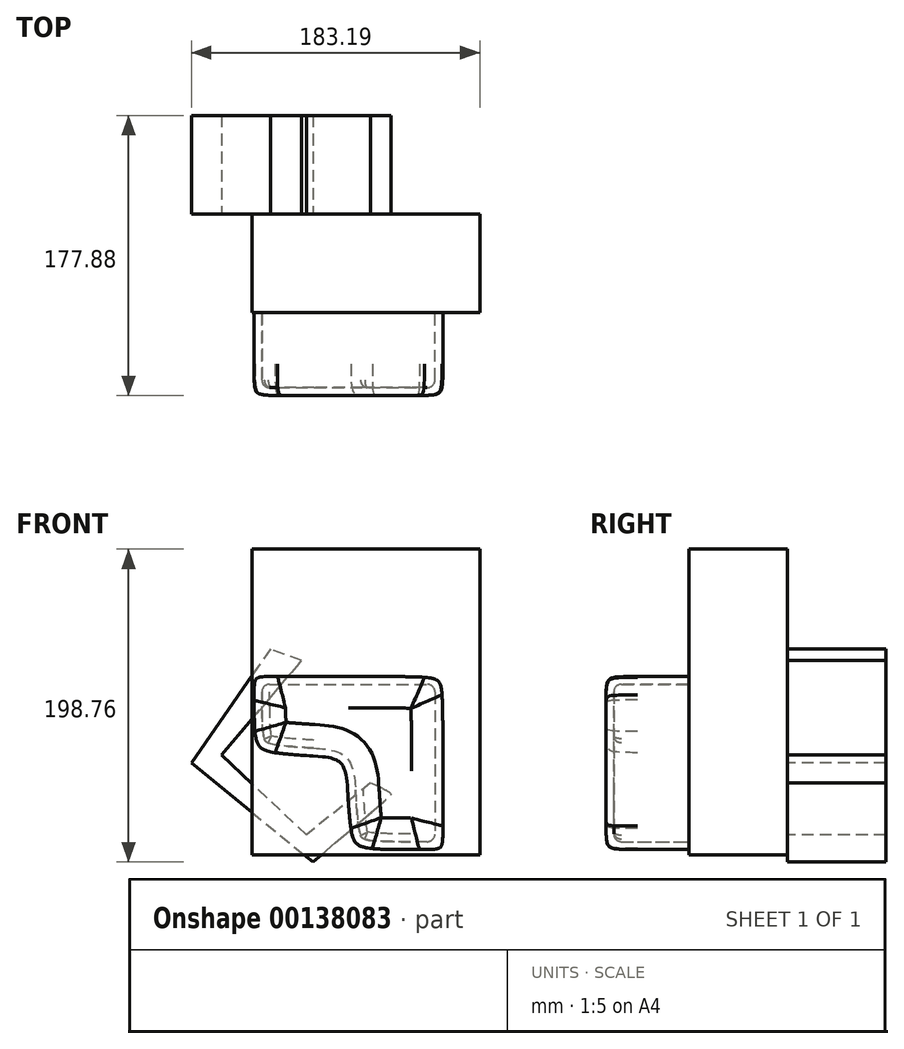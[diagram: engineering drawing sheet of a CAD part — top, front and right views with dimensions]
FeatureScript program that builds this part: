
annotation { "Feature Type Name" : "Feature", "Feature Type Description" : "" }
export const myFeature = defineFeature(function(context is Context, id is Id, definition is map)
    precondition{}
    {
        {
            var Q0;
            Q0=qCreatedBy(makeId("Front.planeOp"),FACE);
            var sketch = newSketch(context, id + "F0", { "sketchPlane" : qUnion([Q0])});
            skLineSegment(sketch, "E0", {"start": v(-60.72, 50) * mm, "end": v(59.28, 50) * mm});
            skLineSegment(sketch, "E1", {"start": v(59.28, 50) * mm, "end": v(59.28, -60) * mm});
            skLineSegment(sketch, "E2", {"start": v(59.28, -60) * mm, "end": v(-0.72, -60) * mm});
            skLineSegment(sketch, "E3", {"start": v(-0.72, -60) * mm, "end": v(-0.72, 0) * mm});
            skLineSegment(sketch, "E4", {"start": v(-0.72, 0) * mm, "end": v(-60.72, 0) * mm});
            skLineSegment(sketch, "E5", {"start": v(-60.72, 0) * mm, "end": v(-60.72, 50) * mm});
            skSolve(sketch);
        }
        {
            var Q0;
            Q0=makeQuery(id+"F0.imprint","IMPRINT",FACE,{"disambiguationData":[TD([[makeQuery(id+"F0.imprint","IMPRINT",EDGE,{"derivedFrom":sQuery(id+"F0.wireOp",EDGE,"E0")}),-1.0]])]});
            extrude(context, id + "F1", {"entities" : qUnion([Q0]), "depth" : 115.18 * mm});
        }
        {
            var Q0;
            Q0=makeQuery(id+"F1.opExtrude","SWEPT_EDGE",EDGE,{"disambiguationData":[OSD([sQuery(id+"F0.wireOp",EDGE,"E3"),sQuery(id+"F0.wireOp",EDGE,"E4")])]});
            fillet(context, id + "F2", {"entities" : qUnion([Q0]), "radius" : 50 * mm, "tangentPropagation" : true, "rho" : .8, "crossSection" : FilletCrossSection.CONIC, "allowEdgeOverflow" : false});
        }
        {
            var Q0;
            Q0=makeQuery(id+"F1.opExtrude","SWEPT_EDGE",EDGE,{"disambiguationData":[OSD([sQuery(id+"F0.wireOp",EDGE,"E2"),sQuery(id+"F0.wireOp",EDGE,"E3")])]});
            fillet(context, id + "F3", {"entities" : qUnion([Q0]), "radius" : 40 * mm, "tangentPropagation" : true, "rho" : .8, "crossSection" : FilletCrossSection.CONIC, "allowEdgeOverflow" : false});
        }
        {
            var Q0;
            Q0=makeQuery(id+"F1.opExtrude","SWEPT_EDGE",EDGE,{"disambiguationData":[OSD([sQuery(id+"F0.wireOp",EDGE,"E4"),sQuery(id+"F0.wireOp",EDGE,"E5")])]});
            fillet(context, id + "F4", {"entities" : qUnion([Q0]), "radius" : 40 * mm, "tangentPropagation" : true, "rho" : .8, "crossSection" : FilletCrossSection.CONIC, "allowEdgeOverflow" : false});
        }
        {
            var Q0;
            Q0=makeQuery(id+"F1.opExtrude","SWEPT_EDGE",EDGE,{"disambiguationData":[OSD([sQuery(id+"F0.wireOp",EDGE,"E0"),sQuery(id+"F0.wireOp",EDGE,"E5")])]});
            fillet(context, id + "F5", {"entities" : qUnion([Q0]), "radius" : 15 * mm, "tangentPropagation" : true, "rho" : .8, "crossSection" : FilletCrossSection.CONIC, "allowEdgeOverflow" : false});
        }
        {
            var Q0;
            Q0=makeQuery(id+"F1.opExtrude","SWEPT_EDGE",EDGE,{"disambiguationData":[OSD([sQuery(id+"F0.wireOp",EDGE,"E1"),sQuery(id+"F0.wireOp",EDGE,"E2")])]});
            fillet(context, id + "F6", {"entities" : qUnion([Q0]), "radius" : 15 * mm, "tangentPropagation" : true, "rho" : .8, "crossSection" : FilletCrossSection.CONIC, "allowEdgeOverflow" : false});
        }
        {
            var Q0;
            Q0=makeQuery(id+"F1.opExtrude","SWEPT_EDGE",EDGE,{"disambiguationData":[OSD([sQuery(id+"F0.wireOp",EDGE,"E0"),sQuery(id+"F0.wireOp",EDGE,"E1")])]});
            fillet(context, id + "F7", {"entities" : qUnion([Q0]), "radius" : 60 * mm, "tangentPropagation" : true, "rho" : .9, "crossSection" : FilletCrossSection.CONIC, "allowEdgeOverflow" : false});
        }
        {
            var Q0;
            {var subQ0=sQuery(id+"F0.wireOp",EDGE,"E5");var subQ1=sQuery(id+"F0.wireOp",EDGE,"E4");Q0=makeQuery(id+"F4.opFillet","BLEND_EDGE",EDGE,{"blendedFrom":[makeQuery(id+"F1.opExtrude","SWEPT_EDGE",EDGE,{"disambiguationData":[OSD([subQ1,subQ0])]}),makeQuery(id+"F1.opExtrude","CAP_FACE",FACE,{"disambiguationData":[OSD([sQuery(id+"F0.wireOp",EDGE,"E0"),sQuery(id+"F0.wireOp",EDGE,"E1"),sQuery(id+"F0.wireOp",EDGE,"E2"),sQuery(id+"F0.wireOp",EDGE,"E3"),subQ1,subQ0])],"isStart":false})],"blendedInto":[makeQuery(id+"F1.opExtrude","CAP_FACE",FACE,{"disambiguationData":[OSD([sQuery(id+"F0.wireOp",EDGE,"E0"),sQuery(id+"F0.wireOp",EDGE,"E1"),sQuery(id+"F0.wireOp",EDGE,"E2"),sQuery(id+"F0.wireOp",EDGE,"E3"),subQ1,subQ0])],"isStart":false})]});}
            fillet(context, id + "F8", {"entities" : qUnion([Q0]), "radius" : 20 * mm, "tangentPropagation" : true, "rho" : .8, "crossSection" : FilletCrossSection.CONIC, "allowEdgeOverflow" : false});
        }
        {
            var Q0;
            Q0=makeQuery(id+"F1.opExtrude","CAP_FACE",FACE,{"disambiguationData":[OSD([sQuery(id+"F0.wireOp",EDGE,"E0"),sQuery(id+"F0.wireOp",EDGE,"E1"),sQuery(id+"F0.wireOp",EDGE,"E2"),sQuery(id+"F0.wireOp",EDGE,"E3"),sQuery(id+"F0.wireOp",EDGE,"E4"),sQuery(id+"F0.wireOp",EDGE,"E5")])],"isStart":true});
            shell(context, id + "F9", {"entities" : qUnion([Q0]), "thickness" : 5 * mm});
        }
        {
            var Q0;
            Q0=makeQuery(id+"F9.opShell","TWEAK_EDGE",EDGE,{"derivedFrom":[makeQuery(id+"F1.opExtrude","SWEPT_FACE",FACE,{"disambiguationData":[OSD([sQuery(id+"F0.wireOp",EDGE,"E0")])]}),makeQuery(id+"F1.opExtrude","SWEPT_FACE",FACE,{"disambiguationData":[OSD([sQuery(id+"F0.wireOp",EDGE,"E1")])]})]});
            fillet(context, id + "F10", {"entities" : qUnion([Q0]), "radius" : 5 * mm, "tangentPropagation" : true, "allowEdgeOverflow" : false});
        }
        {
            var Q0;
            Q0=makeQuery(id+"F9.opShell","TWEAK_EDGE",EDGE,{"derivedFrom":[makeQuery(id+"F4.opFillet","BLEND_FACE",FACE,{"disambiguationData":[OSD([sQuery(id+"F0.wireOp",EDGE,"E4"),sQuery(id+"F0.wireOp",EDGE,"E5")])]}),makeQuery(id+"F1.opExtrude","SWEPT_FACE",FACE,{"disambiguationData":[OSD([sQuery(id+"F0.wireOp",EDGE,"E0")])]})]});
            fillet(context, id + "F11", {"entities" : qUnion([Q0]), "radius" : 5 * mm, "tangentPropagation" : true, "allowEdgeOverflow" : false});
        }
        {
            var Q0;
            Q0=makeQuery(id+"F9.opShell","TWEAK_EDGE",EDGE,{"derivedFrom":[makeQuery(id+"F1.opExtrude","SWEPT_FACE",FACE,{"disambiguationData":[OSD([sQuery(id+"F0.wireOp",EDGE,"E2")])]}),makeQuery(id+"F1.opExtrude","SWEPT_FACE",FACE,{"disambiguationData":[OSD([sQuery(id+"F0.wireOp",EDGE,"E1")])]})]});
            fillet(context, id + "F12", {"entities" : qUnion([Q0]), "radius" : 5 * mm, "tangentPropagation" : true, "allowEdgeOverflow" : false});
        }
        {
            var Q0;
            {var subQ0=sQuery(id+"F0.wireOp",EDGE,"E0");Q0=makeQuery(id+"F9.opShell","TWEAK_EDGE",EDGE,{"derivedFrom":[makeQuery(id+"F1.opExtrude","SWEPT_FACE",FACE,{"disambiguationData":[OSD([subQ0])]}),makeQuery(id+"F1.opExtrude","CAP_FACE",FACE,{"disambiguationData":[OSD([subQ0,sQuery(id+"F0.wireOp",EDGE,"E1"),sQuery(id+"F0.wireOp",EDGE,"E2"),sQuery(id+"F0.wireOp",EDGE,"E3"),sQuery(id+"F0.wireOp",EDGE,"E4"),sQuery(id+"F0.wireOp",EDGE,"E5")])],"isStart":false})]});}
            fillet(context, id + "F13", {"entities" : qUnion([Q0]), "radius" : 5 * mm, "tangentPropagation" : true, "allowEdgeOverflow" : false});
        }
        {
            var Q0;
            Q0=qCreatedBy(makeId("Front.planeOp"),FACE);
            var sketch = newSketch(context, id + "F14", { "sketchPlane" : qUnion([Q0])});
            skLineSegment(sketch, "E6", {"start": v(-50.35, 67.36) * mm, "end": v(-100.41, -5.07) * mm});
            skLineSegment(sketch, "E7", {"start": v(-100.41, -5.07) * mm, "end": v(-23.35, -67.87) * mm});
            skLineSegment(sketch, "E8", {"start": v(-23.35, -67.87) * mm, "end": v(27.82, -24.42) * mm});
            skLineSegment(sketch, "E9", {"start": v(27.82, -24.42) * mm, "end": v(13.37, -17.67) * mm});
            skLineSegment(sketch, "E10", {"start": v(13.37, -17.67) * mm, "end": v(-27.43, -50.7) * mm});
            skLineSegment(sketch, "E11", {"start": v(-27.43, -50.7) * mm, "end": v(-81.28, 0) * mm});
            skLineSegment(sketch, "E12", {"start": v(-81.28, 0) * mm, "end": v(-30.47, 60) * mm});
            skLineSegment(sketch, "E13", {"start": v(-30.47, 60) * mm, "end": v(-50.35, 67.36) * mm});
            skSolve(sketch);
        }
        {
            var Q0;
            Q0=makeQuery(id+"F14.imprint","IMPRINT",FACE,{"disambiguationData":[TD([[makeQuery(id+"F14.imprint","IMPRINT",EDGE,{"derivedFrom":sQuery(id+"F14.wireOp",EDGE,"E6")}),1.0]])]});
            extrude(context, id + "F15", {"entities" : qUnion([Q0]), "operationType" : NewBodyOperationType.ADD, "oppositeDirection" : true, "depth" : 62.7 * mm});
        }
        {
            var Q0;
            Q0=qCreatedBy(makeId("Front.planeOp"),FACE);
            var sketch = newSketch(context, id + "F16", { "sketchPlane" : qUnion([Q0])});
            skLineSegment(sketch, "E14.bottom", {"start": v(82.78, 130.89) * mm, "end": v(-61.9, 130.89) * mm});
            skLineSegment(sketch, "E14.top", {"start": v(82.78, -63.22) * mm, "end": v(-61.9, -63.22) * mm});
            skLineSegment(sketch, "E14.left", {"start": v(82.78, 130.89) * mm, "end": v(82.78, -63.22) * mm});
            skLineSegment(sketch, "E14.right", {"start": v(-61.9, 130.89) * mm, "end": v(-61.9, -63.22) * mm});
            skPoint(sketch, "E14.middle", {"position": v(10.44, 33.83) * mm});
            skSolve(sketch);
        }
        {
            var Q0;
            Q0 = qSketchRegion(id + "F16", true);
            extrude(context, id + "F17", {"entities" : qUnion([Q0]), "operationType" : NewBodyOperationType.ADD, "depth" : 62.4 * mm});
        }
        {
            var Q0;
            Q0=makeQuery(id+"F15.opExtrude","SWEPT_EDGE",EDGE,{"disambiguationData":[OSD([sQuery(id+"F14.wireOp",EDGE,"E8"),sQuery(id+"F14.wireOp",EDGE,"E9")])]});
            fillet(context, id + "F18", {"entities" : qUnion([Q0]), "radius" : 5 * mm, "tangentPropagation" : true, "rho" : .75, "crossSection" : FilletCrossSection.CONIC, "allowEdgeOverflow" : false});
        }
    });
